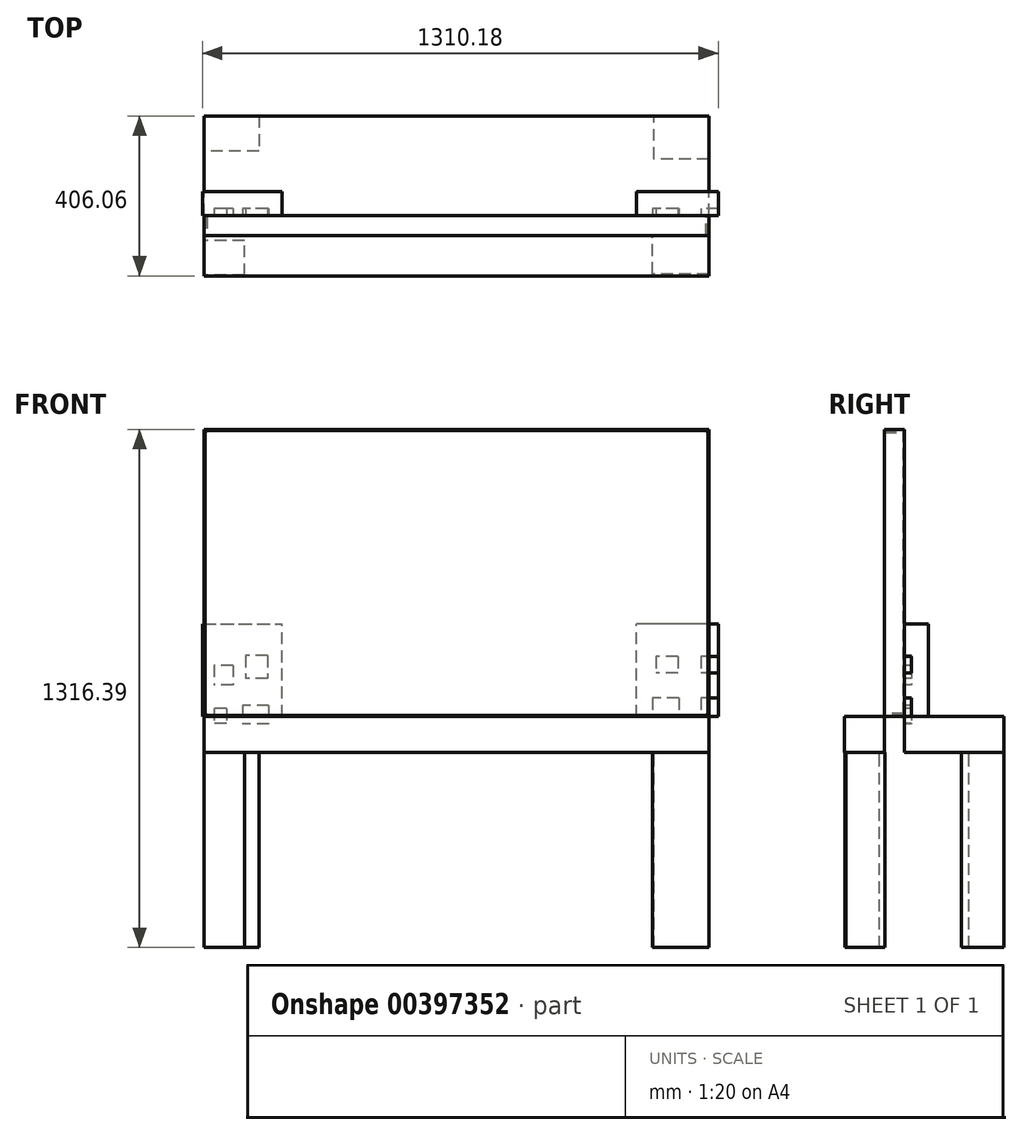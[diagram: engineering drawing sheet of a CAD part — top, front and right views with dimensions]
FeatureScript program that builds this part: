
annotation { "Feature Type Name" : "Feature", "Feature Type Description" : "" }
export const myFeature = defineFeature(function(context is Context, id is Id, definition is map)
    precondition{}
    {
        {
            var Q0;
            Q0=qCreatedBy(makeId("Front.planeOp"),FACE);
            var sketch = newSketch(context, id + "F0", { "sketchPlane" : qUnion([Q0])});
            skLineSegment(sketch, "E0.bottom", {"start": v(-23.77, 0) * mm, "end": v(-1306.53, 0) * mm});
            skLineSegment(sketch, "E0.top", {"start": v(-23.77, 729.65) * mm, "end": v(-1306.53, 729.65) * mm});
            skLineSegment(sketch, "E0.left", {"start": v(-23.77, 0) * mm, "end": v(-23.77, 729.65) * mm});
            skLineSegment(sketch, "E0.right", {"start": v(-1306.53, 0) * mm, "end": v(-1306.53, 729.65) * mm});
            skSolve(sketch);
        }
        {
            var Q0;
            Q0=makeQuery(id+"F0.imprint","IMPRINT",FACE,{"disambiguationData":[TD([[makeQuery(id+"F0.imprint","IMPRINT",EDGE,{"derivedFrom":sQuery(id+"F0.wireOp",EDGE,"E0.bottom")}),-1.0]])]});
            extrude(context, id + "F1", {"entities" : qUnion([Q0]), "depth" : 50.8 * mm});
        }
        {
            var Q0;
            Q0=makeQuery(id+"F1.opExtrude","CAP_FACE",FACE,{"disambiguationData":[OSD([sQuery(id+"F0.wireOp",EDGE,"E0.bottom"),sQuery(id+"F0.wireOp",EDGE,"E0.top"),sQuery(id+"F0.wireOp",EDGE,"E0.left"),sQuery(id+"F0.wireOp",EDGE,"E0.right")])],"isStart":false});
            shell(context, id + "F2", {"entities" : qUnion([Q0]), "thickness" : 2.54 * mm});
        }
        {
            var Q0;
            Q0=makeQuery(id+"F2.opShell","OFFSET_EDGE",EDGE,{"disambiguationData":[OSD([sQuery(id+"F0.wireOp",EDGE,"E0.top"),sQuery(id+"F0.wireOp",EDGE,"E0.right")])]});
            var Q1;
            Q1=makeQuery(id+"F2.opShell","OFFSET_EDGE",EDGE,{"disambiguationData":[OSD([sQuery(id+"F0.wireOp",EDGE,"E0.top"),sQuery(id+"F0.wireOp",EDGE,"E0.left")])]});
            var Q2;
            Q2=makeQuery(id+"F2.opShell","OFFSET_EDGE",EDGE,{"disambiguationData":[OSD([sQuery(id+"F0.wireOp",EDGE,"E0.bottom"),sQuery(id+"F0.wireOp",EDGE,"E0.right")])]});
            var Q3;
            Q3=makeQuery(id+"F2.opShell","OFFSET_EDGE",EDGE,{"disambiguationData":[OSD([sQuery(id+"F0.wireOp",EDGE,"E0.bottom"),sQuery(id+"F0.wireOp",EDGE,"E0.left")])]});
            chamfer(context, id + "F3", {"entities" : qUnion([Q0, Q1, Q2, Q3]), "width" : 5.08 * mm, "tangentPropagation" : true});
        }
        {
            var Q0;
            Q0=makeQuery(id+"F1.opExtrude","SWEPT_FACE",FACE,{"disambiguationData":[OSD([sQuery(id+"F0.wireOp",EDGE,"E0.bottom")])]});
            var sketch = newSketch(context, id + "F4", { "sketchPlane" : qUnion([Q0])});
            skPoint(sketch, "E1.oppositeSnap0", {"position": v(-23.77, 25.4) * mm});
            skLineSegment(sketch, "E1.bottom", {"start": v(-1306.53, 153.15) * mm, "end": v(-23.77, 153.15) * mm});
            skLineSegment(sketch, "E1.top", {"start": v(-1306.53, -252.91) * mm, "end": v(-23.77, -252.91) * mm});
            skLineSegment(sketch, "E1.left", {"start": v(-1306.53, 153.15) * mm, "end": v(-1306.53, -252.91) * mm});
            skLineSegment(sketch, "E1.right", {"start": v(-23.77, 153.15) * mm, "end": v(-23.77, -252.91) * mm});
            skSolve(sketch);
        }
        {
            var Q0;
            {var subQ0=sQuery(id+"F4.wireOp",EDGE,"E1.top");Q0=makeQuery(id+"F4.imprint","IMPRINT",FACE,{"disambiguationData":[TD([[makeQuery(id+"F4.imprint","IMPRINT",EDGE,{"derivedFrom":subQ0}),1.0]])]});}
            var Q1;
            {var subQ0=sQuery(id+"F4.wireOp",EDGE,"E1.bottom");Q1=makeQuery(id+"F4.imprint","IMPRINT",FACE,{"disambiguationData":[TD([[makeQuery(id+"F4.imprint","IMPRINT",EDGE,{"derivedFrom":subQ0}),-1.0]])]});}
            extrude(context, id + "F5", {"entities" : qUnion([Q0, Q1]), "depth" : 91.44 * mm});
        }
        {
            var Q0;
            Q0=makeQuery(id+"F5.opExtrude","CAP_FACE",FACE,{"disambiguationData":[OSD([sQuery(id+"F0.wireOp",EDGE,"E0.bottom"),sQuery(id+"F4.wireOp",EDGE,"E1.top"),sQuery(id+"F4.wireOp",EDGE,"E1.left"),sQuery(id+"F4.wireOp",EDGE,"E1.right")])],"isStart":false});
            var sketch = newSketch(context, id + "F6", { "sketchPlane" : qUnion([Q0])});
            skLineSegment(sketch, "E2.bottom", {"start": v(-23.3, 148.73) * mm, "end": v(-167.29, 148.73) * mm});
            skLineSegment(sketch, "E2.top", {"start": v(-23.3, 50.4) * mm, "end": v(-167.29, 50.4) * mm});
            skLineSegment(sketch, "E2.left", {"start": v(-23.3, 148.73) * mm, "end": v(-23.3, 50.4) * mm});
            skLineSegment(sketch, "E2.right", {"start": v(-167.29, 148.73) * mm, "end": v(-167.29, 50.4) * mm});
            skLineSegment(sketch, "E3.bottom", {"start": v(-23.77, -144.05) * mm, "end": v(-163.68, -144.05) * mm});
            skLineSegment(sketch, "E3.top", {"start": v(-23.77, -252.91) * mm, "end": v(-163.68, -252.91) * mm});
            skLineSegment(sketch, "E3.left", {"start": v(-23.77, -144.05) * mm, "end": v(-23.77, -252.91) * mm});
            skLineSegment(sketch, "E3.right", {"start": v(-163.68, -144.05) * mm, "end": v(-163.68, -252.91) * mm});
            skLineSegment(sketch, "E4.bottom", {"start": v(-1167.11, -252.91) * mm, "end": v(-1306.53, -252.91) * mm});
            skLineSegment(sketch, "E4.top", {"start": v(-1167.11, -163.31) * mm, "end": v(-1306.53, -163.31) * mm});
            skLineSegment(sketch, "E4.left", {"start": v(-1167.11, -252.91) * mm, "end": v(-1167.11, -163.31) * mm});
            skLineSegment(sketch, "E4.right", {"start": v(-1306.53, -252.91) * mm, "end": v(-1306.53, -163.31) * mm});
            skLineSegment(sketch, "E5.bottom", {"start": v(-1203.67, 151.76) * mm, "end": v(-1306.53, 151.76) * mm});
            skLineSegment(sketch, "E5.top", {"start": v(-1203.67, 64.11) * mm, "end": v(-1306.53, 64.11) * mm});
            skLineSegment(sketch, "E5.left", {"start": v(-1203.67, 151.76) * mm, "end": v(-1203.67, 64.11) * mm});
            skLineSegment(sketch, "E5.right", {"start": v(-1306.53, 151.76) * mm, "end": v(-1306.53, 64.11) * mm});
            skSolve(sketch);
        }
        {
            var Q0;
            Q0=makeQuery(id+"F6.imprint","IMPRINT",FACE,{"disambiguationData":[TD([[makeQuery(id+"F6.imprint","IMPRINT",EDGE,{"derivedFrom":sQuery(id+"F6.wireOp",EDGE,"E5.bottom")}),1.0]])]});
            var Q1;
            Q1=makeQuery(id+"F6.imprint","IMPRINT",FACE,{"disambiguationData":[TD([[makeQuery(id+"F6.imprint","IMPRINT",EDGE,{"derivedFrom":sQuery(id+"F6.wireOp",EDGE,"E3.bottom")}),1.0]])]});
            var Q2;
            Q2=makeQuery(id+"F6.imprint","IMPRINT",FACE,{"disambiguationData":[TD([[makeQuery(id+"F6.imprint","IMPRINT",EDGE,{"derivedFrom":sQuery(id+"F6.wireOp",EDGE,"E4.bottom")}),1.0]])]});
            var Q3;
            Q3=makeQuery(id+"F6.imprint","IMPRINT",FACE,{"disambiguationData":[TD([[makeQuery(id+"F6.imprint","IMPRINT",EDGE,{"derivedFrom":sQuery(id+"F6.wireOp",EDGE,"E2.bottom")}),1.0]])]});
            extrude(context, id + "F7", {"entities" : qUnion([Q0, Q1, Q2, Q3]), "depth" : 495.3 * mm});
        }
        {
            var Q0;
            Q0=qCreatedBy(makeId("Front.planeOp"),FACE);
            var sketch = newSketch(context, id + "F8", { "sketchPlane" : qUnion([Q0])});
            skLineSegment(sketch, "E6.bottom", {"start": v(0, 0) * mm, "end": v(-207.6, 0) * mm});
            skLineSegment(sketch, "E6.top", {"start": v(0, 235.1) * mm, "end": v(-207.6, 235.1) * mm});
            skLineSegment(sketch, "E6.left", {"start": v(0, 0) * mm, "end": v(0, 235.1) * mm});
            skLineSegment(sketch, "E6.right", {"start": v(-207.6, 0) * mm, "end": v(-207.6, 235.1) * mm});
            skLineSegment(sketch, "E7.bottom", {"start": v(-1310.18, 0) * mm, "end": v(-1108.41, 0) * mm});
            skLineSegment(sketch, "E7.top", {"start": v(-1310.18, 235.1) * mm, "end": v(-1108.41, 235.1) * mm});
            skLineSegment(sketch, "E7.left", {"start": v(-1310.18, 0) * mm, "end": v(-1310.18, 235.1) * mm});
            skLineSegment(sketch, "E7.right", {"start": v(-1108.41, 0) * mm, "end": v(-1108.41, 235.1) * mm});
            skSolve(sketch);
        }
        {
            var Q0;
            Q0 = qSketchRegion(id + "F8", true);
            extrude(context, id + "F9", {"entities" : qUnion([Q0]), "oppositeDirection" : true, "depth" : 60.96 * mm});
        }
        {
            var Q0;
            Q0=qCreatedBy(makeId("Front.planeOp"),FACE);
            var sketch = newSketch(context, id + "F10", { "sketchPlane" : qUnion([Q0])});
            skLineSegment(sketch, "E8.bottom", {"start": v(0, 152.76) * mm, "end": v(-44.26, 152.76) * mm});
            skLineSegment(sketch, "E8.top", {"start": v(0, 110.32) * mm, "end": v(-44.26, 110.32) * mm});
            skLineSegment(sketch, "E8.left", {"start": v(0, 152.76) * mm, "end": v(0, 110.32) * mm});
            skLineSegment(sketch, "E8.right", {"start": v(-44.26, 152.76) * mm, "end": v(-44.26, 110.32) * mm});
            skLineSegment(sketch, "E9.bottom", {"start": v(-103.06, 152.08) * mm, "end": v(-158.36, 152.08) * mm});
            skLineSegment(sketch, "E9.top", {"start": v(-103.06, 110.32) * mm, "end": v(-158.36, 110.32) * mm});
            skLineSegment(sketch, "E9.left", {"start": v(-103.06, 152.08) * mm, "end": v(-103.06, 110.32) * mm});
            skLineSegment(sketch, "E9.right", {"start": v(-158.36, 152.08) * mm, "end": v(-158.36, 110.32) * mm});
            skLineSegment(sketch, "E10.bottom", {"start": v(0, 47.18) * mm, "end": v(-44.26, 47.18) * mm});
            skLineSegment(sketch, "E10.top", {"start": v(0, 0) * mm, "end": v(-44.26, 0) * mm});
            skLineSegment(sketch, "E10.left", {"start": v(0, 47.18) * mm, "end": v(0, 0) * mm});
            skLineSegment(sketch, "E10.right", {"start": v(-44.26, 47.18) * mm, "end": v(-44.26, 0) * mm});
            skLineSegment(sketch, "E11.bottom", {"start": v(-100.14, 47.18) * mm, "end": v(-167.56, 47.18) * mm});
            skLineSegment(sketch, "E11.top", {"start": v(-100.14, 0) * mm, "end": v(-167.56, 0) * mm});
            skLineSegment(sketch, "E11.left", {"start": v(-100.14, 47.18) * mm, "end": v(-100.14, 0) * mm});
            skLineSegment(sketch, "E11.right", {"start": v(-167.56, 47.18) * mm, "end": v(-167.56, 0) * mm});
            skLineSegment(sketch, "E12.bottom", {"start": v(-1145.4, 155.02) * mm, "end": v(-1201.27, 155.02) * mm});
            skLineSegment(sketch, "E12.top", {"start": v(-1145.4, 96.59) * mm, "end": v(-1201.27, 96.59) * mm});
            skLineSegment(sketch, "E12.left", {"start": v(-1145.4, 155.02) * mm, "end": v(-1145.4, 96.59) * mm});
            skLineSegment(sketch, "E12.right", {"start": v(-1201.27, 155.02) * mm, "end": v(-1201.27, 96.59) * mm});
            skLineSegment(sketch, "E13.bottom", {"start": v(-1232.55, 130.26) * mm, "end": v(-1280.92, 130.26) * mm});
            skLineSegment(sketch, "E13.top", {"start": v(-1232.55, 80.5) * mm, "end": v(-1280.92, 80.5) * mm});
            skLineSegment(sketch, "E13.left", {"start": v(-1232.55, 130.26) * mm, "end": v(-1232.55, 80.5) * mm});
            skLineSegment(sketch, "E13.right", {"start": v(-1280.92, 130.26) * mm, "end": v(-1280.92, 80.5) * mm});
            skLineSegment(sketch, "E14.bottom", {"start": v(-1142.28, 28.2) * mm, "end": v(-1207.97, 28.2) * mm});
            skLineSegment(sketch, "E14.top", {"start": v(-1142.28, -18.56) * mm, "end": v(-1207.97, -18.56) * mm});
            skLineSegment(sketch, "E14.left", {"start": v(-1142.28, 28.2) * mm, "end": v(-1142.28, -18.56) * mm});
            skLineSegment(sketch, "E14.right", {"start": v(-1207.97, 28.2) * mm, "end": v(-1207.97, -18.56) * mm});
            skLineSegment(sketch, "E15.bottom", {"start": v(-1249.44, 20.2) * mm, "end": v(-1280.92, 20.2) * mm});
            skLineSegment(sketch, "E15.top", {"start": v(-1249.44, -17.16) * mm, "end": v(-1280.92, -17.16) * mm});
            skLineSegment(sketch, "E15.left", {"start": v(-1249.44, 20.2) * mm, "end": v(-1249.44, -17.16) * mm});
            skLineSegment(sketch, "E15.right", {"start": v(-1280.92, 20.2) * mm, "end": v(-1280.92, -17.16) * mm});
            skSolve(sketch);
        }
        {
            var Q0;
            Q0 = qSketchRegion(id + "F10", true);
            extrude(context, id + "F11", {"entities" : qUnion([Q0]), "oppositeDirection" : true, "depth" : 17.78 * mm});
        }
    });
